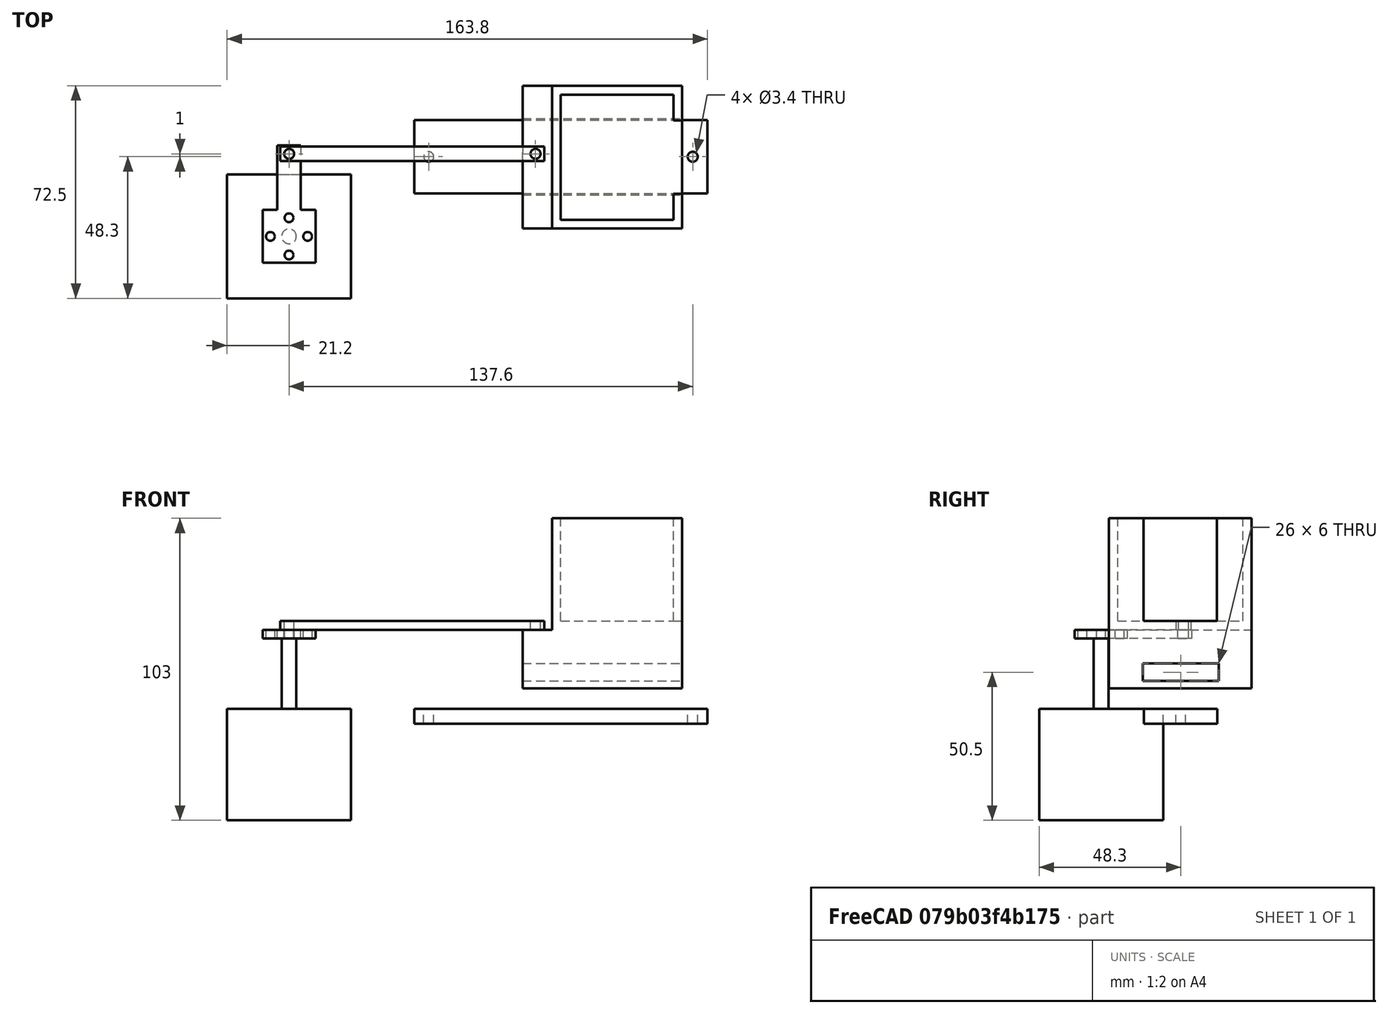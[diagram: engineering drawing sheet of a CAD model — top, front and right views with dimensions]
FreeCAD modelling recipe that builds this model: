
FCSTD DOCUMENT  (FreeCAD 0.18R16131 (Git))
Label: SliderAlt
License: All rights reserved
LicenseURL: http://en.wikipedia.org/wiki/All_rights_reserved
objects: Part::Cut×12, Part::Box×10, Part::Cylinder×10, Part::MultiFuse×4
note: 36 computed .brp shape members not serialized (recipe doc carries the construction recipe); baked Part::Feature solids carry a one-line shape summary decoded from their .brp

FEATURE [Part::Box] Box  label="TrayNegative"
  AttacherType = Attacher::AttachEngine3D
  Height = 35
  Length = 38.4
  Width = 42.7
FEATURE [Part::Box] Box001  label="Tray"
  AttacherType = Attacher::AttachEngine3D
  Height = 38
  Length = 44.4
  Placement = pos=(-3,-3,-3) rot=(0,0,1;0rad)
  Width = 48.7
FEATURE [Part::Cut] Cut  label="MainTray"
  Base = -> Box001
  Tool = -> Box
FEATURE [Part::Box] Box002  label="TrayRightCutout"
  AttacherType = Attacher::AttachEngine3D
  Height = 35
  Length = 3
  Placement = pos=(38.4,8.85,0) rot=(0,0,1;0rad)
  Width = 25
FEATURE [Part::Cut] Cut001  label="CircularMotorTray"
  Base = -> Cut
  Placement = pos=(0,0,5) rot=(0,0,1;0rad)
  Tool = -> Box002
FEATURE [Part::Box] Box003  label="TrayBase"
  AttacherType = Attacher::AttachEngine3D
  Height = 20
  Length = 54.4
  Placement = pos=(-13,-3,-18) rot=(0,0,1;0rad)
  Width = 48.7
FEATURE [Part::Box] Box004  label="TraySlider"
  AttacherType = Attacher::AttachEngine3D
  Height = 5
  Length = 100
  Placement = pos=(-50,9,-30) rot=(0,0,1;0rad)
  Width = 25
FEATURE [Part::Box] Box005  label="TraySliderCutout"
  AttacherType = Attacher::AttachEngine3D
  Height = 6
  Length = 100
  Placement = pos=(-50,8.5,-15.5) rot=(0,0,1;0rad)
  Width = 26
FEATURE [Part::Cut] Cut002  label="HollowHolder"
  Base = -> Box003
  Tool = -> Box005
FEATURE [Part::MultiFuse] Fusion
  Shapes = -> [Cut001,Cut002]
FEATURE [Part::Box] Box014  label="SliderArm"
  AttacherType = Attacher::AttachEngine3D
  Height = 3
  Length = 90
  Width = 5
FEATURE [Part::Cylinder] Cylinder015
  Angle = 360
  AttacherType = Attacher::AttachEngine3D
  Height = 10
  Placement = pos=(87,2.5,0) rot=(0,0,1;0rad)
  Radius = 1.7
FEATURE [Part::Cylinder] Cylinder014
  Angle = 360
  AttacherType = Attacher::AttachEngine3D
  Height = 10
  Placement = pos=(3,2.5,0) rot=(0,0,1;0rad)
  Radius = 1.7
FEATURE [Part::Cut] Cut016
  Base = -> Box014
  Tool = -> Cylinder014
FEATURE [Part::Cut] Cut015  label="SlideArm"
  Base = -> Cut016
  Placement = pos=(-95.6,20,2) rot=(0,0,1;0rad)
  Tool = -> Cylinder015
FEATURE [Part::Box] Box013  label="SlideMotorArmExt"
  AttacherType = Attacher::AttachEngine3D
  Height = 3
  Length = 8
  Placement = pos=(1,-1,0) rot=(0,0,1;0rad)
  Width = 22
FEATURE [Part::Cylinder] Cylinder008  label="Rotor001"
  Angle = 360
  AttacherType = Attacher::AttachEngine3D
  Height = 24
  Placement = pos=(21.15,21.15,38) rot=(0,0,1;0rad)
  Radius = 2.5
FEATURE [Part::Cylinder] Cylinder011
  Angle = 360
  AttacherType = Attacher::AttachEngine3D
  Height = 10
  Placement = pos=(5,2,0) rot=(0,0,1;0rad)
  Radius = 1.8
FEATURE [Part::Cut] Cut013
  Base = -> Box013
  Tool = -> Cylinder011
FEATURE [Part::Cylinder] Cylinder009
  Angle = 360
  AttacherType = Attacher::AttachEngine3D
  Height = 10
  Placement = pos=(-1.35,30,0) rot=(0,0,1;0rad)
  Radius = 1.5
FEATURE [Part::Box] Box011  label="Motor001"
  AttacherType = Attacher::AttachEngine3D
  Height = 38
  Length = 42.3
  Width = 42.3
FEATURE [Part::MultiFuse] Fusion004  label="17HS4401-2"
  Placement = pos=(69,97,-48) rot=(1,0,0;1.5708rad)
  Shapes = -> [Box011,Cylinder008]
FEATURE [Part::Cylinder] Cylinder010
  Angle = 360
  AttacherType = Attacher::AttachEngine3D
  Height = 10
  Placement = pos=(5,23.65,0) rot=(0,0,1;0rad)
  Radius = 1.5
FEATURE [Part::Cylinder] Cylinder012
  Angle = 360
  AttacherType = Attacher::AttachEngine3D
  Height = 10
  Placement = pos=(11.35,30,0) rot=(0,0,1;0rad)
  Radius = 1.5
FEATURE [Part::Cylinder] Cylinder013
  Angle = 360
  AttacherType = Attacher::AttachEngine3D
  Height = 10
  Placement = pos=(5,36.35,0) rot=(0,0,1;0rad)
  Radius = 1.5
FEATURE [Part::Box] Box012  label="SlideMotorArm"
  AttacherType = Attacher::AttachEngine3D
  Height = 3
  Length = 18
  Placement = pos=(-4,21,0) rot=(0,0,1;0rad)
  Width = 18
FEATURE [Part::Cut] Cut010
  Base = -> Box012
  Tool = -> Cylinder013
FEATURE [Part::Cut] Cut012
  Base = -> Cut010
  Tool = -> Cylinder012
FEATURE [Part::Cut] Cut011
  Base = -> Cut012
  Tool = -> Cylinder009
FEATURE [Part::Cut] Cut014
  Base = -> Cut011
  Tool = -> Cylinder010
FEATURE [Part::MultiFuse] Fusion005  label="SlideMotorArmExtension"
  Placement = pos=(60.15,35,-21.85) rot=(0.57735,0.57735,-0.57735;2.0944rad)
  Shapes = -> [Cut014,Cut013]
FEATURE [Part::MultiFuse] Fusion006  label="SlidingMotorConfig"
  Placement = pos=(-65.8,84.5,34) rot=(0.57735,-0.57735,0.57735;4.18879rad)
  Shapes = -> [Fusion004,Fusion005]
FEATURE [Part::Cylinder] Cylinder
  Angle = 360
  AttacherType = Attacher::AttachEngine3D
  Height = 10
  Placement = pos=(-45,21.5,-33) rot=(0,0,1;0rad)
  Radius = 1.7
FEATURE [Part::Cut] Cut017
  Base = -> Box004
  Tool = -> Cylinder
FEATURE [Part::Cylinder] Cylinder016
  Angle = 360
  AttacherType = Attacher::AttachEngine3D
  Height = 10
  Placement = pos=(45,21.5,-33) rot=(0,0,1;0rad)
  Radius = 1.7
FEATURE [Part::Cut] Cut018  label="TraySliderV2"
  Base = -> Cut017
  Tool = -> Cylinder016
